# Revit family: Sink-Vessel-Lavatory-KALLISTA-Obidos-P72061
name_source: partatom
category: Plumbing Fixtures
units: mm (PartAtom-declared; Revit-internal decimal feet)

## family parameters
Cut with Voids When Loaded = No
Host = Face
Maintain Annotation Orientation = No
OmniClass Number = 23.31.13.00
OmniClass Title = Sinks
Part Type = Normal
Room Calculation Point = No
Round Connector Dimension = Use Diameter
Shared = No

## types (2) — shared parameters
ADA Compliant = No
Assembly Code = D2010400
CW Connection = No
Cold Water Inlet = Cold Water Inlet
Date Modified = 06/20/2025
Default Elevation = 36"
Description = Decorative Vessel
Drain Included = No
HW Connection = No
Height = 6"
Hot Water Inlet = Hot Water Inlet
Length = 15 3/4"
Manufacturer = Kallista Co.
Master Format 2014 = 22 41 16
Master Format 2014 Name = Residential Lavatories and Sinks
Material = Cast Bronze
Product Documentation Link = https://techcomm.kohler.com
Product Name = Obidos
Product Page URL = https://www.kallista.com
URL = https://www.kallista.com
Vent Connection = No
Waste Connection = Yes
Waste Water Outlet = Waste Water Outlet
WaterSense Certified = No
Width = 10 7/8"

## per-type parameters (varying)
| type | Finish | Model | Type |
| TBR-Traditional Bronze | Kallista-Cast_Bronze-TBR-Traditional_Bronze | P72061-00-TBR | 1 |
| WHB-White Satin Bronze | Kallista-Cast_Bronze-WHB-White_Satin_Bronze | P72061-00-WHB | 2 |

## geometry (parser evidence)
native form markers: Sweep x4
no freeform markers — native parametric forms only
